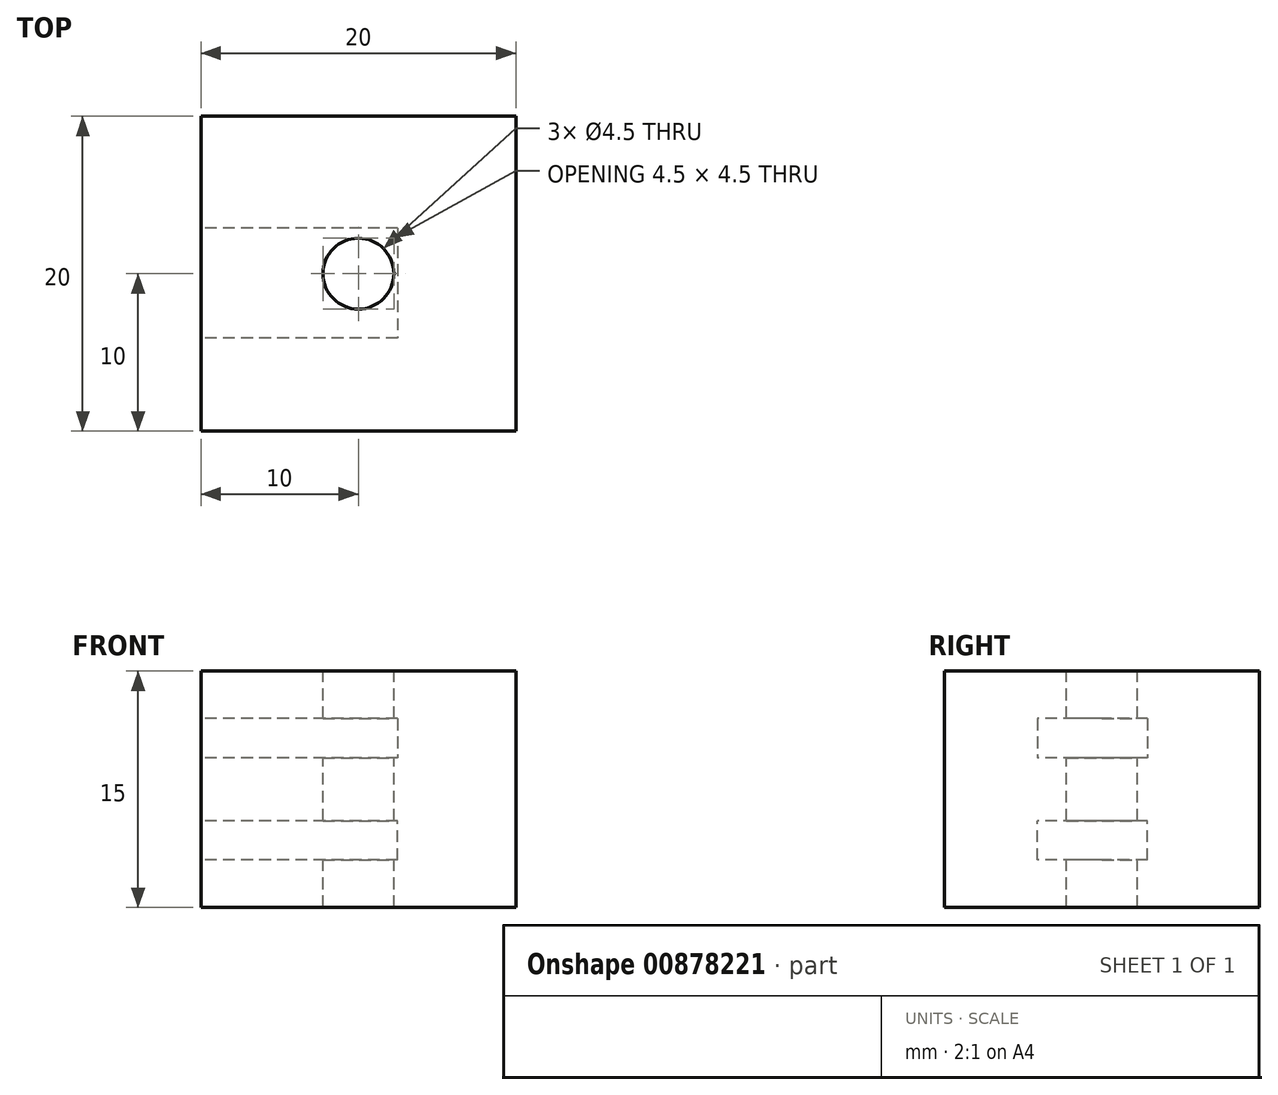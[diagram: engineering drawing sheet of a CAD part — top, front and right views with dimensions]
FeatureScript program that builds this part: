
annotation { "Feature Type Name" : "Feature", "Feature Type Description" : "" }
export const myFeature = defineFeature(function(context is Context, id is Id, definition is map)
    precondition{}
    {
        {
            var Q0;
            Q0=qCreatedBy(makeId("Top.planeOp"),FACE);
            var sketch = newSketch(context, id + "F0", { "sketchPlane" : qUnion([Q0])});
            skLineSegment(sketch, "E0.bottom", {"start": v(10, -10) * mm, "end": v(-10, -10) * mm});
            skLineSegment(sketch, "E0.top", {"start": v(10, 10) * mm, "end": v(-10, 10) * mm});
            skLineSegment(sketch, "E0.left", {"start": v(10, -10) * mm, "end": v(10, 10) * mm});
            skLineSegment(sketch, "E0.right", {"start": v(-10, -10) * mm, "end": v(-10, 10) * mm});
            skPoint(sketch, "E0.middle", {"position": v(0, 0) * mm});
            skSolve(sketch);
        }
        {
            var Q0;
            Q0 = qSketchRegion(id + "F0", true);
            extrude(context, id + "F1", {"entities" : qUnion([Q0]), "depth" : 15 * mm, "offsetDistance" : 25 * mm});
        }
        {
            var Q0;
            Q0=makeQuery(id+"F1.opExtrude","CAP_FACE",FACE,{"disambiguationData":[OSD([sQuery(id+"F0.wireOp",EDGE,"E0.bottom"),sQuery(id+"F0.wireOp",EDGE,"E0.top"),sQuery(id+"F0.wireOp",EDGE,"E0.left"),sQuery(id+"F0.wireOp",EDGE,"E0.right")])],"isStart":false});
            var sketch = newSketch(context, id + "F2", { "sketchPlane" : qUnion([Q0])});
            skCircle(sketch, "E1", {"center": v(0, 0) * mm, "radius": 2.25 * mm});
            skSolve(sketch);
        }
        {
            var Q0;
            Q0 = qSketchRegion(id + "F2", true);
            extrude(context, id + "F3", {"entities" : qUnion([Q0]), "operationType" : NewBodyOperationType.REMOVE, "endBound" : BoundingType.THROUGH_ALL, "oppositeDirection" : true, "depth" : 25 * mm, "offsetDistance" : 25 * mm});
        }
        {
            var Q0;
            Q0=makeQuery(id+"F1.opExtrude","SWEPT_FACE",FACE,{"disambiguationData":[OSD([sQuery(id+"F0.wireOp",EDGE,"E0.right")])]});
            var sketch = newSketch(context, id + "F4", { "sketchPlane" : qUnion([Q0])});
            skLineSegment(sketch, "E2.bottom", {"start": v(-2.9, 3) * mm, "end": v(4.1, 3) * mm});
            skLineSegment(sketch, "E2.top", {"start": v(-2.9, 5.5) * mm, "end": v(4.1, 5.5) * mm});
            skLineSegment(sketch, "E2.left", {"start": v(-2.9, 3) * mm, "end": v(-2.9, 5.5) * mm});
            skLineSegment(sketch, "E2.right", {"start": v(4.1, 3) * mm, "end": v(4.1, 5.5) * mm});
            skLineSegment(sketch, "E3", {"start": v(-13.92, 7.5) * mm, "end": v(16.78, 7.5) * mm, "construction": true});
            skLineSegment(sketch, "E4.MirrorCS", {"start": v(-2.9, 9.5) * mm, "end": v(4.1, 9.5) * mm});
            skLineSegment(sketch, "E5.MirrorCS", {"start": v(4.1, 12) * mm, "end": v(4.1, 9.5) * mm});
            skLineSegment(sketch, "E6.MirrorCS", {"start": v(-2.9, 12) * mm, "end": v(4.1, 12) * mm});
            skLineSegment(sketch, "E7.MirrorCS", {"start": v(-2.9, 12) * mm, "end": v(-2.9, 9.5) * mm});
            skSolve(sketch);
        }
        {
            var Q0;
            Q0 = qSketchRegion(id + "F4", true);
            extrude(context, id + "F5", {"entities" : qUnion([Q0]), "operationType" : NewBodyOperationType.REMOVE, "oppositeDirection" : true, "depth" : 12.5 * mm, "offsetDistance" : 25 * mm});
        }
    });
